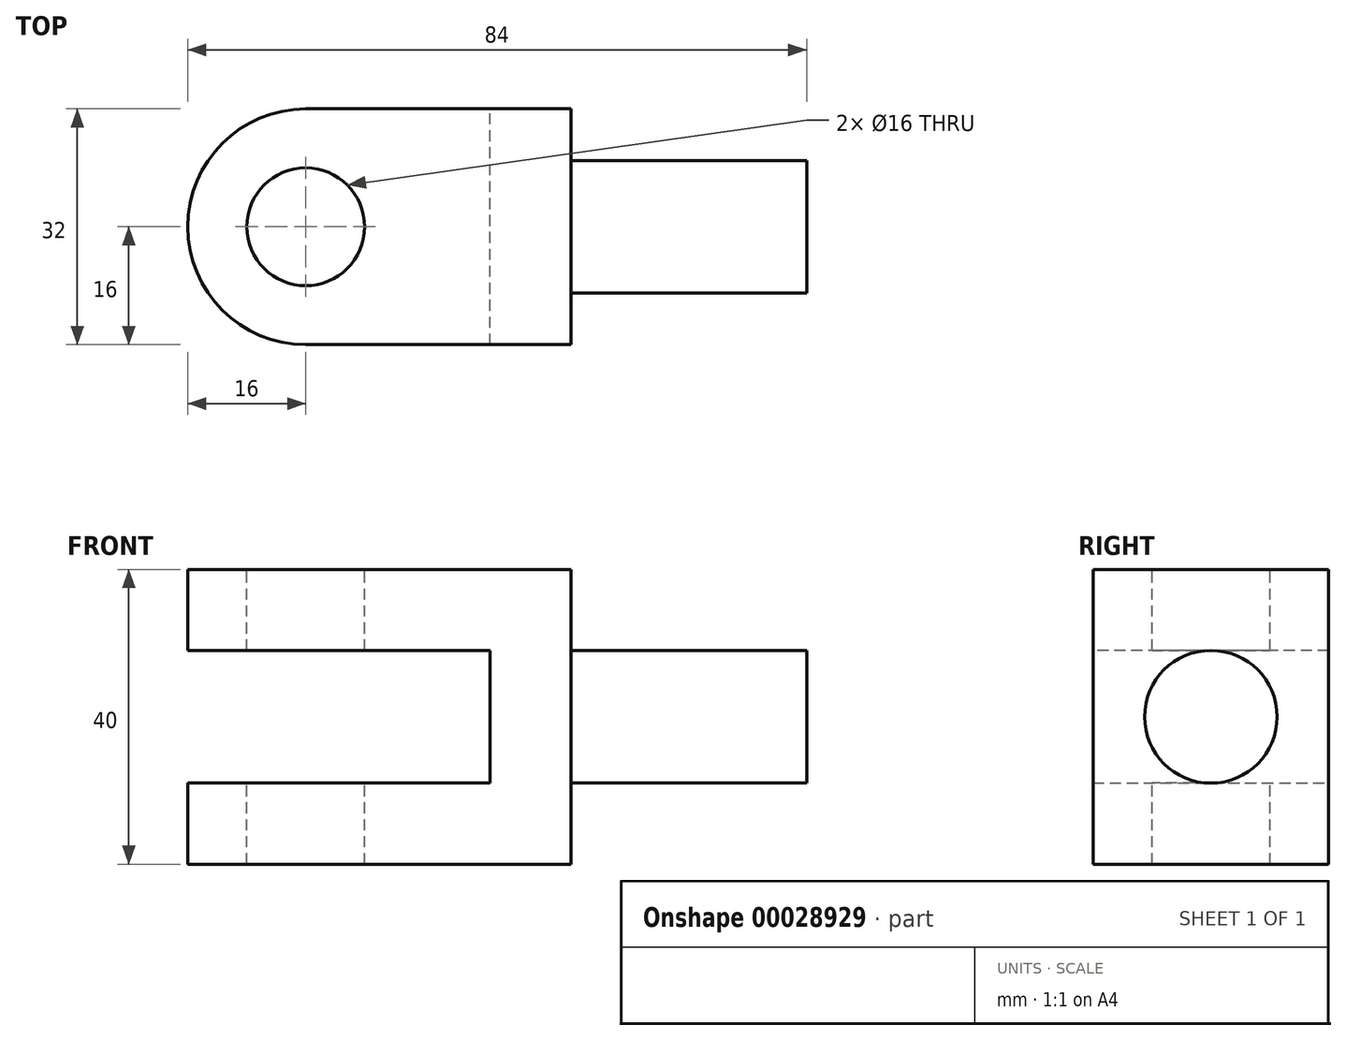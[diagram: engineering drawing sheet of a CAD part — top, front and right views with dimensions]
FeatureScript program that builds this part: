
annotation { "Feature Type Name" : "Feature", "Feature Type Description" : "" }
export const myFeature = defineFeature(function(context is Context, id is Id, definition is map)
    precondition{}
    {
        {
            var Q0;
            Q0=qCreatedBy(makeId("Right.planeOp"),FACE);
            var sketch = newSketch(context, id + "F0", { "sketchPlane" : qUnion([Q0])});
            skCircle(sketch, "E0", {"center": v(0, 0) * mm, "radius": 9 * mm});
            skSolve(sketch);
        }
        {
            var Q0;
            Q0 = qSketchRegion(id + "F0", true);
            extrude(context, id + "F1", {"entities" : qUnion([Q0]), "depth" : 32 * mm});
        }
        {
            var Q0;
            Q0=qCreatedBy(makeId("Front.planeOp"),FACE);
            var sketch = newSketch(context, id + "F2", { "sketchPlane" : qUnion([Q0])});
            skLineSegment(sketch, "E1", {"start": v(0, 0) * mm, "end": v(0, 20) * mm, "construction": true});
            skLineSegment(sketch, "E2", {"start": v(0, 20) * mm, "end": v(-52, 20) * mm, "construction": true});
            skLineSegment(sketch, "E3", {"start": v(-52, 20) * mm, "end": v(-52, 9) * mm, "construction": true});
            skLineSegment(sketch, "E4", {"start": v(-52, 9) * mm, "end": v(-11, 9) * mm, "construction": true});
            skLineSegment(sketch, "E5", {"start": v(-11, 9) * mm, "end": v(-11, 0) * mm, "construction": true});
            skLineSegment(sketch, "E6.MirrorCS", {"start": v(-11, -9) * mm, "end": v(-11, 0) * mm, "construction": true});
            skLineSegment(sketch, "E7.MirrorCS", {"start": v(-52, -9) * mm, "end": v(-11, -9) * mm, "construction": true});
            skLineSegment(sketch, "E8.MirrorCS", {"start": v(-52, -20) * mm, "end": v(-52, -9) * mm, "construction": true});
            skLineSegment(sketch, "E9.MirrorCS", {"start": v(0, 0) * mm, "end": v(0, -20) * mm, "construction": true});
            skLineSegment(sketch, "E10.MirrorCS", {"start": v(0, -20) * mm, "end": v(-52, -20) * mm, "construction": true});
            skLineSegment(sketch, "E11", {"start": v(0, -20) * mm, "end": v(0, 20) * mm});
            skLineSegment(sketch, "E12", {"start": v(0, 20) * mm, "end": v(-52, 20) * mm});
            skLineSegment(sketch, "E13", {"start": v(-52, 20) * mm, "end": v(-52, 9) * mm});
            skLineSegment(sketch, "E14", {"start": v(-52, 9) * mm, "end": v(-11, 9) * mm});
            skLineSegment(sketch, "E15", {"start": v(-11, 9) * mm, "end": v(-11, -9) * mm});
            skLineSegment(sketch, "E16", {"start": v(-11, -9) * mm, "end": v(-52, -9) * mm});
            skLineSegment(sketch, "E17", {"start": v(-52, -9) * mm, "end": v(-52, -20) * mm});
            skLineSegment(sketch, "E18", {"start": v(-52, -20) * mm, "end": v(0, -20) * mm});
            skSolve(sketch);
        }
        {
            var Q0;
            Q0=makeQuery(id+"F2.imprint","IMPRINT",FACE,{"disambiguationData":[TD([[makeQuery(id+"F2.imprint","IMPRINT",EDGE,{"derivedFrom":sQuery(id+"F2.wireOp",EDGE,"E11")}),1.0]])]});
            extrude(context, id + "F3", {"entities" : qUnion([Q0]), "operationType" : NewBodyOperationType.ADD, "endBound" : BoundingType.SYMMETRIC, "depth" : 32 * mm});
        }
        {
            var Q0;
            Q0=makeQuery(id+"F3.opExtrude","SWEPT_FACE",FACE,{"disambiguationData":[OSD([sQuery(id+"F2.wireOp",EDGE,"E12")])]});
            var sketch = newSketch(context, id + "F4", { "sketchPlane" : qUnion([Q0])});
            skArc(sketch, "E19", {"start": v(-36, 16) * mm, "mid": v(-52, 0) * mm, "end": v(-36, -16) * mm});
            skSolve(sketch);
        }
        {
            var Q0;
            {var subQ0=sQuery(id+"F2.wireOp",EDGE,"E12");var subQ1=makeQuery(id+"F3.opExtrude","CAP_EDGE",EDGE,{"disambiguationData":[OSD([subQ0])],"isStart":true});var subQ2=sQuery(id+"F4.wireOp",EDGE,"E19");var subQ3=makeQuery(id+"F4.imprint","INTERSECT",VERTEX,{"derivedFrom":[subQ1,subQ2]});Q0=makeQuery(id+"F4.imprint","IMPRINT",FACE,{"disambiguationData":[TD([[makeQuery(id+"F4.imprint","IMPRINT",EDGE,{"disambiguationData":[TD([[subQ3,-1.0]])],"derivedFrom":subQ2}),-1.0]])]});}
            var Q1;
            {var subQ0=sQuery(id+"F2.wireOp",EDGE,"E12");var subQ1=makeQuery(id+"F3.opExtrude","CAP_EDGE",EDGE,{"disambiguationData":[OSD([subQ0])],"isStart":false});var subQ2=sQuery(id+"F4.wireOp",EDGE,"E19");var subQ3=makeQuery(id+"F4.imprint","INTERSECT",VERTEX,{"derivedFrom":[subQ1,subQ2]});Q1=makeQuery(id+"F4.imprint","IMPRINT",FACE,{"disambiguationData":[TD([[makeQuery(id+"F4.imprint","IMPRINT",EDGE,{"disambiguationData":[TD([[subQ3,1.0]])],"derivedFrom":subQ2}),-1.0]])]});}
            extrude(context, id + "F5", {"entities" : qUnion([Q0, Q1]), "operationType" : NewBodyOperationType.REMOVE, "endBound" : BoundingType.THROUGH_ALL, "oppositeDirection" : true, "depth" : 25 * mm, "hasSecondDirection" : true, "secondDirectionBound" : SecondDirectionBoundingType.THROUGH_ALL, "secondDirectionOppositeDirection" : false, "secondDirectionDepth" : 25 * mm});
        }
        {
            var Q0;
            Q0=makeQuery(id+"F3.opExtrude","SWEPT_FACE",FACE,{"disambiguationData":[OSD([sQuery(id+"F2.wireOp",EDGE,"E12")])]});
            var sketch = newSketch(context, id + "F6", { "sketchPlane" : qUnion([Q0])});
            skCircle(sketch, "E20", {"center": v(-36, 0) * mm, "radius": 8 * mm});
            skSolve(sketch);
        }
        {
            var Q0;
            Q0=makeQuery(id+"F6.imprint","IMPRINT",FACE,{"disambiguationData":[TD([[makeQuery(id+"F6.imprint","IMPRINT",EDGE,{"derivedFrom":sQuery(id+"F6.wireOp",EDGE,"E20")}),1.0]])]});
            extrude(context, id + "F7", {"entities" : qUnion([Q0]), "operationType" : NewBodyOperationType.REMOVE, "endBound" : BoundingType.THROUGH_ALL, "oppositeDirection" : true, "depth" : 10 * mm});
        }
    });
